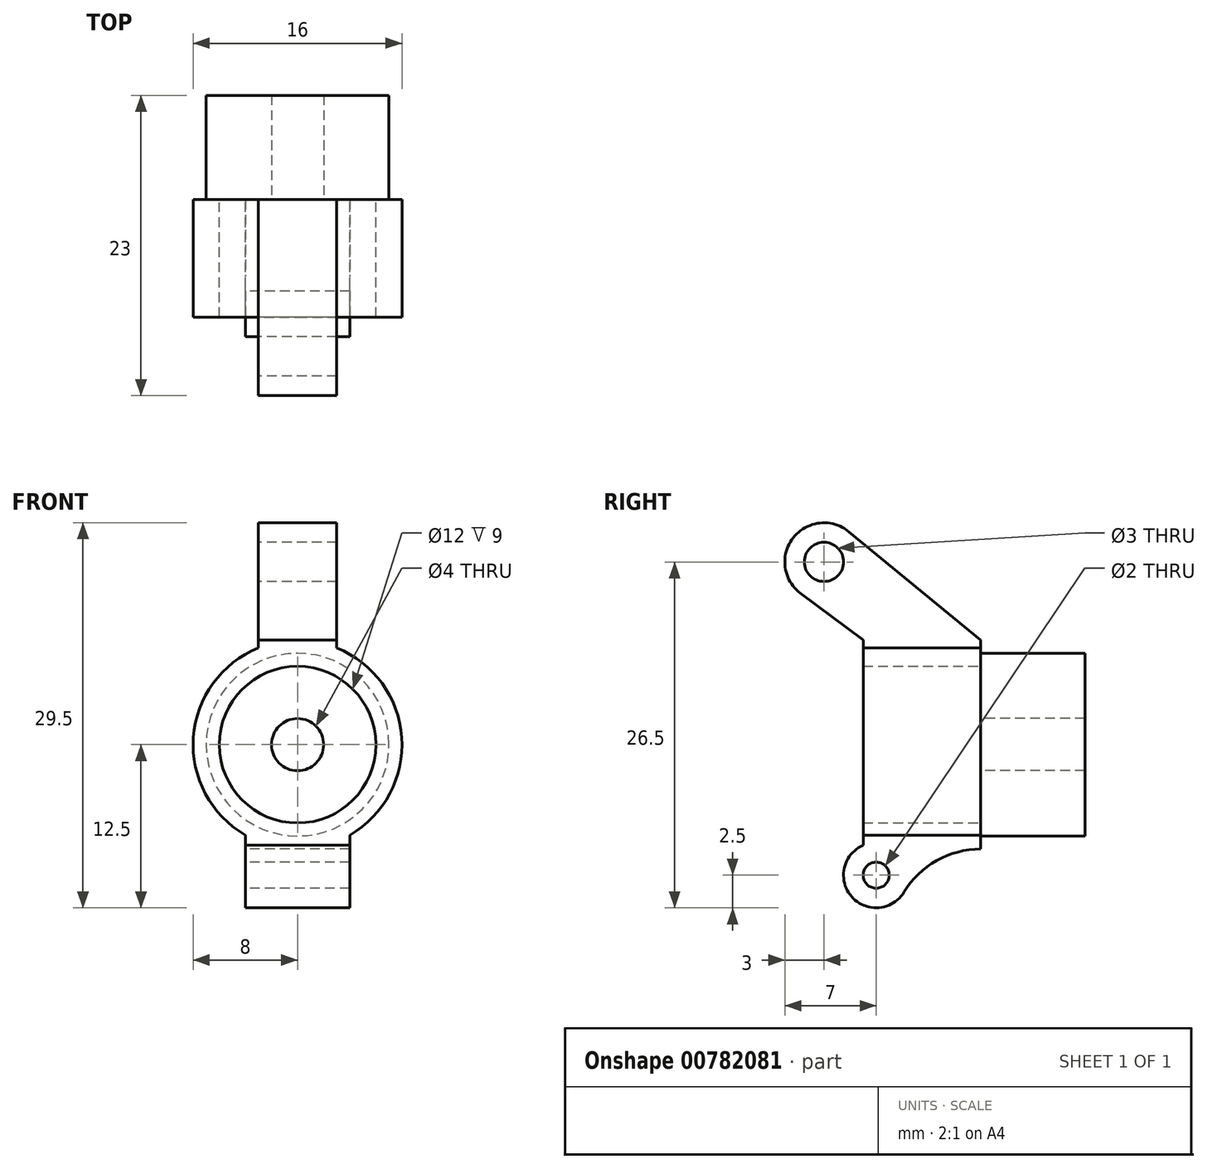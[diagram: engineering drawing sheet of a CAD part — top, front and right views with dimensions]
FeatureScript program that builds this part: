
annotation { "Feature Type Name" : "Feature", "Feature Type Description" : "" }
export const myFeature = defineFeature(function(context is Context, id is Id, definition is map)
    precondition{}
    {
        {
            var Q0;
            Q0=qCreatedBy(makeId("Front.planeOp"),FACE);
            var sketch = newSketch(context, id + "F0", { "sketchPlane" : qUnion([Q0])});
            skArc(sketch, "E0", {"start": v(8, 0) * mm, "mid": v(0, 8) * mm, "end": v(-8, 0) * mm});
            skCircle(sketch, "E1", {"center": v(0, 0) * mm, "radius": 6 * mm});
            skLineSegment(sketch, "E2", {"start": v(0, 0) * mm, "end": v(9.88, 0) * mm, "construction": true});
            skLineSegment(sketch, "E3", {"start": v(0, 0) * mm, "end": v(0, 9.34) * mm, "construction": true});
            skLineSegment(sketch, "E4.MirrorCS", {"start": v(0, 0) * mm, "end": v(-9.88, 0) * mm, "construction": true});
            skArc(sketch, "E5.trimOffspring", {"start": v(-8, 0) * mm, "mid": v(0, -8) * mm, "end": v(8, 0) * mm});
            skPoint(sketch, "E6.end.orphan", {"position": v(7.5, 4) * mm});
            skPoint(sketch, "E6.start.orphan", {"position": v(8, 0) * mm});
            skPoint(sketch, "E7.MirrorCS.end.orphan", {"position": v(7.5, -4) * mm});
            skPoint(sketch, "E8.MirrorCS.start.orphan", {"position": v(-8, 0) * mm});
            skPoint(sketch, "E9.MirrorCS.start.orphan", {"position": v(-7.5, 4) * mm});
            skPoint(sketch, "E10.MirrorCS.start.orphan", {"position": v(-7.5, -4) * mm});
            skSolve(sketch);
        }
        {
            var Q0;
            Q0=qSketchRegion(id+"F0",true);
            extrude(context, id + "F1", {"entities" : qUnion([Q0]), "depth" : 9 * mm, "symmetric" : true});
        }
        {
            var Q0;
            Q0=makeQuery(id+"FDlZR3japZBE9mr_1.boolean.opBoolean","MERGE",FACE,{"derivedFrom":[makeQuery(id+"F1.opExtrude","CAP_FACE",FACE,{"disambiguationData":[OSD([sQuery(id+"F0.wireOp",EDGE,"E0"),sQuery(id+"F0.wireOp",EDGE,"E1"),sQuery(id+"F0.wireOp",EDGE,"E6"),sQuery(id+"F0.wireOp",EDGE,"bKShqBVs-TCg5-hqsg-2Zin-jb4kYLIbsAUQ"),sQuery(id+"F0.wireOp",EDGE,"E8.MirrorCS"),sQuery(id+"F0.wireOp",EDGE,"E9.MirrorCS"),sQuery(id+"F0.wireOp",EDGE,"E7.MirrorCS"),sQuery(id+"F0.wireOp",EDGE,"0079e600-e878-4d57-aa4f-ef33ea1a4fac0.MirrorCS"),sQuery(id+"F0.wireOp",EDGE,"f6fc4373-7105-42fd-a591-3c9390de6fbc0.MirrorCS"),sQuery(id+"F0.wireOp",EDGE,"E10.MirrorCS"),sQuery(id+"F0.wireOp",EDGE,"E5.trimOffspring")])],"isStart":true}),makeQuery(id+"FDlZR3japZBE9mr_1.opExtrude","SWEPT_FACE",FACE,{"disambiguationData":[OSD([sQuery(id+"FTksZrnYcWv5Ukm_1.wireOp",EDGE,"x4EYb6om-VWKb-oGQX-4Byi-Ye5M8WNYVBj3")])]})]});
            var sketch = newSketch(context, id + "F2", { "sketchPlane" : qUnion([Q0])});
            skCircle(sketch, "E11", {"center": v(0, 0) * mm, "radius": 7 * mm});
            skCircle(sketch, "E12", {"center": v(0, 0) * mm, "radius": 2 * mm});
            skSolve(sketch);
        }
        {
            var Q0;
            Q0=qSketchRegion(id+"F2",true);
            extrude(context, id + "F3", {"entities" : qUnion([Q0]), "operationType" : NewBodyOperationType.ADD, "depth" : 8 * mm});
        }
        {
            var Q0;
            Q0=qCreatedBy(makeId("Right.planeOp"),FACE);
            var sketch = newSketch(context, id + "F4", { "sketchPlane" : qUnion([Q0])});
            skCircle(sketch, "E13", {"center": v(-7.5, 14) * mm, "radius": 1.5 * mm});
            skArc(sketch, "E14", {"start": v(-5.6, 16.32) * mm, "mid": v(-9.86, 15.85) * mm, "end": v(-9.3, 11.6) * mm});
            skLineSegment(sketch, "E15", {"start": v(-4.5, 6) * mm, "end": v(-4.5, 8) * mm});
            skLineSegment(sketch, "E16", {"start": v(-4.5, 8) * mm, "end": v(-9.3, 11.6) * mm});
            skLineSegment(sketch, "E17", {"start": v(-5.6, 16.32) * mm, "end": v(4.5, 8) * mm});
            skLineSegment(sketch, "E18", {"start": v(4.5, 8) * mm, "end": v(4.5, 6) * mm});
            skLineSegment(sketch, "E19", {"start": v(4.5, 6) * mm, "end": v(-4.5, 6) * mm});
            skSolve(sketch);
        }
        {
            var Q0;
            Q0=qSketchRegion(id+"F4",true);
            extrude(context, id + "F5", {"entities" : qUnion([Q0]), "operationType" : NewBodyOperationType.ADD, "depth" : 6 * mm, "symmetric" : true});
        }
        {
            var Q0;
            Q0=qCreatedBy(makeId("Right.planeOp"),FACE);
            var sketch = newSketch(context, id + "F6", { "sketchPlane" : qUnion([Q0])});
            skCircle(sketch, "E20", {"center": v(-3.5, -10) * mm, "radius": 1 * mm});
            skArc(sketch, "E21", {"start": v(-4.5, -7.7) * mm, "mid": v(-5.38, -11.64) * mm, "end": v(-1.36, -11.3) * mm});
            skArc(sketch, "E22", {"start": v(4.5, -8) * mm, "mid": v(1.14, -8.88) * mm, "end": v(-1.36, -11.3) * mm});
            skLineSegment(sketch, "E23", {"start": v(4.5, -8) * mm, "end": v(4.5, -6) * mm});
            skLineSegment(sketch, "E24", {"start": v(4.5, -6) * mm, "end": v(-4.5, -6) * mm});
            skLineSegment(sketch, "E25", {"start": v(-4.5, -6) * mm, "end": v(-4.5, -7.7) * mm});
            skLineSegment(sketch, "E26", {"start": v(4.5, -8) * mm, "end": v(3.66, -8) * mm, "construction": true});
            skSolve(sketch);
        }
        {
            var Q0;
            Q0=qSketchRegion(id+"F6",true);
            extrude(context, id + "F7", {"entities" : qUnion([Q0]), "operationType" : NewBodyOperationType.ADD, "depth" : 8 * mm, "symmetric" : true});
        }
    });
